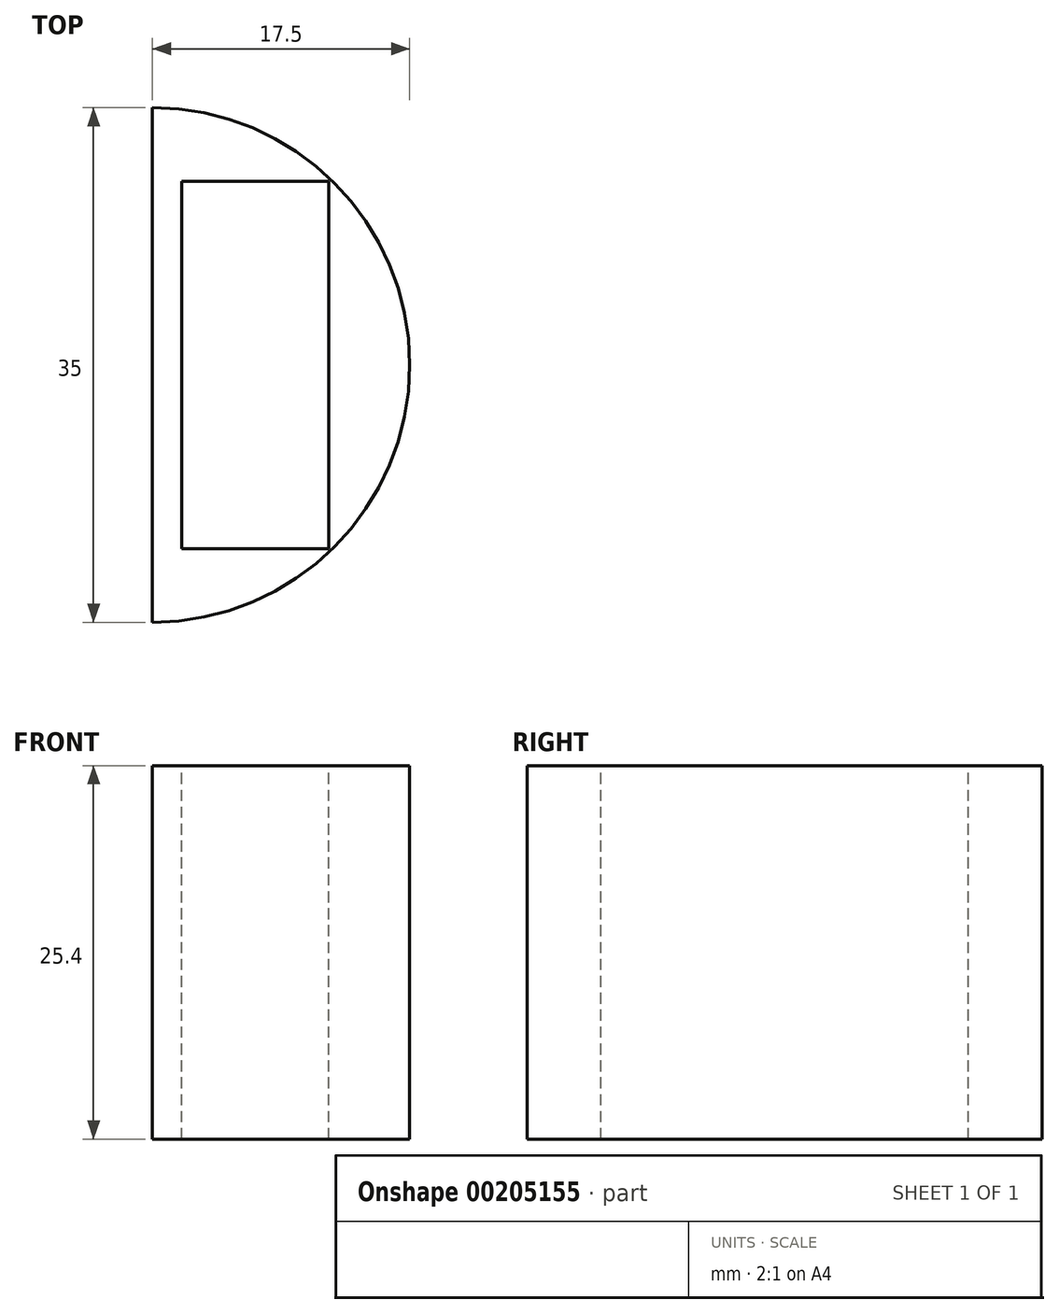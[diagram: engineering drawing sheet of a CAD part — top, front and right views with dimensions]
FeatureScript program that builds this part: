
annotation { "Feature Type Name" : "Feature", "Feature Type Description" : "" }
export const myFeature = defineFeature(function(context is Context, id is Id, definition is map)
    precondition{}
    {
        {
            var Q0;
            Q0=qCreatedBy(makeId("Top.planeOp"),FACE);
            var sketch = newSketch(context, id + "F0", { "sketchPlane" : qUnion([Q0])});
            skCircle(sketch, "E0", {"center": v(0, 0) * mm, "radius": 17.5 * mm});
            skSolve(sketch);
        }
        {
            var Q0;
            Q0 = qSketchRegion(id + "F0", true);
            extrude(context, id + "F1", {"entities" : qUnion([Q0]), "depth" : 25.4 * mm});
        }
        {
            var Q0;
            Q0=qCreatedBy(makeId("Right.planeOp"),FACE);
            var sketch = newSketch(context, id + "F2", { "sketchPlane" : qUnion([Q0])});
            skLineSegment(sketch, "E1.bottom", {"start": v(30.39, 36.76) * mm, "end": v(-30.39, 36.76) * mm});
            skLineSegment(sketch, "E1.top", {"start": v(30.39, -6.41) * mm, "end": v(-30.39, -6.41) * mm});
            skLineSegment(sketch, "E1.left", {"start": v(30.39, 36.76) * mm, "end": v(30.39, -6.41) * mm});
            skLineSegment(sketch, "E1.right", {"start": v(-30.39, 36.76) * mm, "end": v(-30.39, -6.41) * mm});
            skPoint(sketch, "E1.middle", {"position": v(0, 15.17) * mm});
            skSolve(sketch);
        }
        {
            var Q0;
            Q0 = qSketchRegion(id + "F2", true);
            extrude(context, id + "F3", {"entities" : qUnion([Q0]), "operationType" : NewBodyOperationType.REMOVE, "oppositeDirection" : true, "depth" : 25.4 * mm});
        }
        {
            var Q0;
            Q0=makeQuery(id+"F1.opExtrude","CAP_FACE",FACE,{"disambiguationData":[OSD([sQuery(id+"F0.wireOp",EDGE,"E0")])],"isStart":false});
            var sketch = newSketch(context, id + "F4", { "sketchPlane" : qUnion([Q0])});
            skLineSegment(sketch, "E2.bottom", {"start": v(12, 12.5) * mm, "end": v(2, 12.5) * mm});
            skLineSegment(sketch, "E2.top", {"start": v(12, -12.5) * mm, "end": v(2, -12.5) * mm});
            skLineSegment(sketch, "E2.left", {"start": v(12, 12.5) * mm, "end": v(12, -12.5) * mm});
            skLineSegment(sketch, "E2.right", {"start": v(2, 12.5) * mm, "end": v(2, -12.5) * mm});
            skPoint(sketch, "E2.middle", {"position": v(7, 0) * mm});
            skSolve(sketch);
        }
        {
            var Q0;
            Q0 = qSketchRegion(id + "F4", true);
            extrude(context, id + "F5", {"entities" : qUnion([Q0]), "operationType" : NewBodyOperationType.REMOVE, "oppositeDirection" : true, "depth" : 40 * mm});
        }
    });
